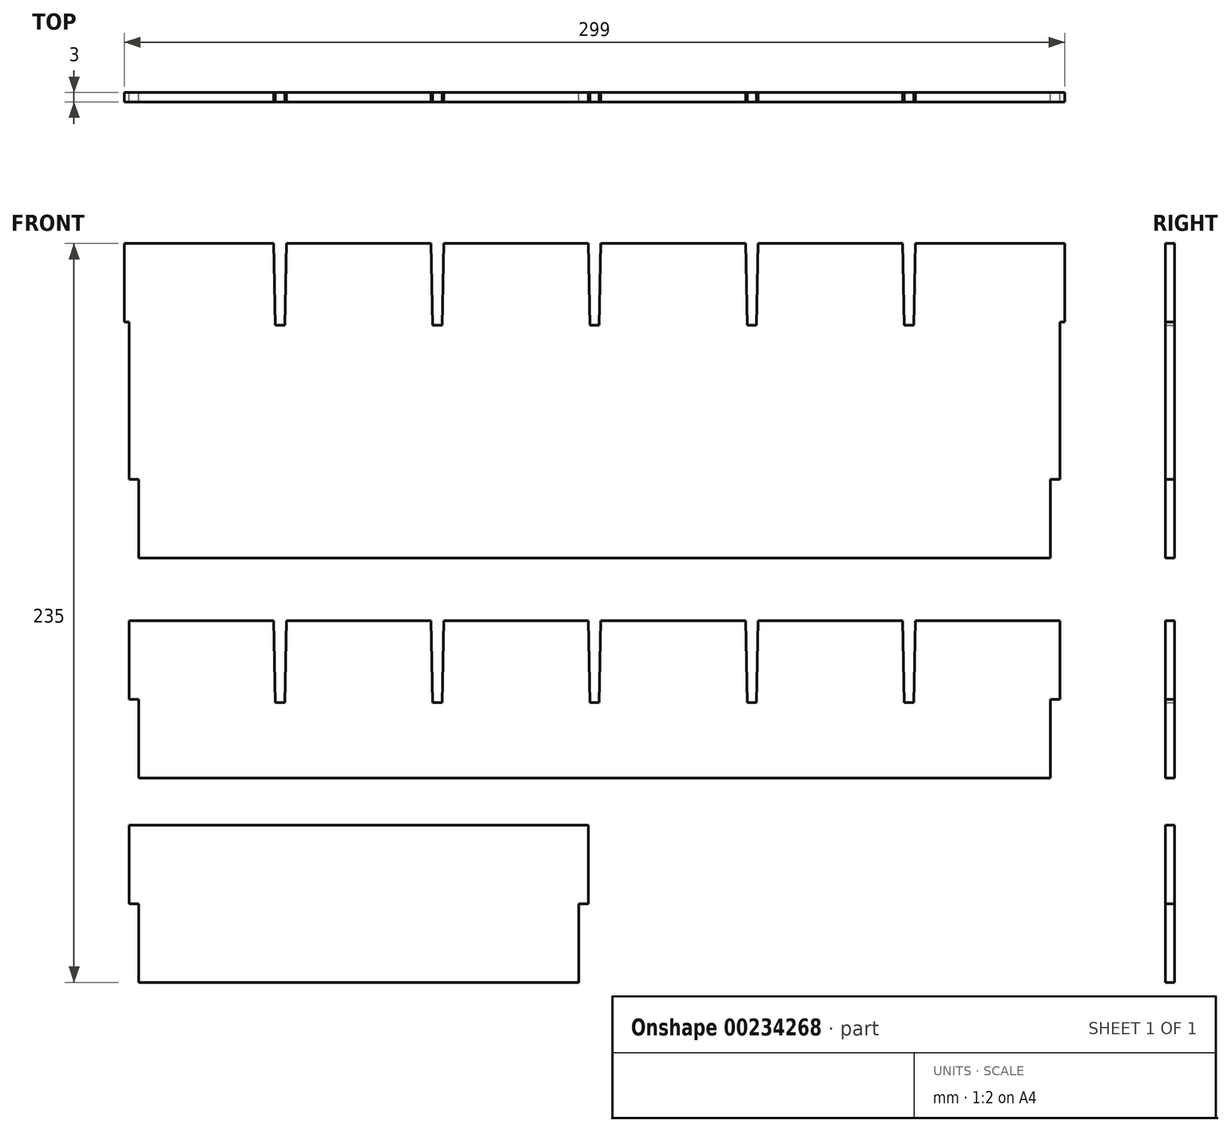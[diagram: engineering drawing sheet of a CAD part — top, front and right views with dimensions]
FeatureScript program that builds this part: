
annotation { "Feature Type Name" : "Feature", "Feature Type Description" : "" }
export const myFeature = defineFeature(function(context is Context, id is Id, definition is map)
    precondition{}
    {
        {
            var Q0;
            Q0=qCreatedBy(makeId("Front.planeOp"),FACE);
            var sketch = newSketch(context, id + "F0", { "sketchPlane" : qUnion([Q0])});
            skLineSegment(sketch, "E0.bottom", {"start": v(10, 10) * mm, "end": v(300, 10) * mm});
            skLineSegment(sketch, "E0.top", {"start": v(10, 110) * mm, "end": v(300, 110) * mm});
            skLineSegment(sketch, "E0.left", {"start": v(10, 10) * mm, "end": v(10, 110) * mm});
            skLineSegment(sketch, "E0.right", {"start": v(300, 10) * mm, "end": v(300, 110) * mm});
            skLineSegment(sketch, "E1", {"start": v(10, 84) * mm, "end": v(300, 84) * mm, "construction": true});
            skLineSegment(sketch, "E2", {"start": v(53, 110) * mm, "end": v(53.5, 84) * mm});
            skLineSegment(sketch, "E3", {"start": v(56.5, 84) * mm, "end": v(57, 110) * mm});
            skLineSegment(sketch, "E4", {"start": v(53, 110) * mm, "end": v(57, 110) * mm});
            skLineSegment(sketch, "E5", {"start": v(53.5, 84) * mm, "end": v(56.5, 84) * mm});
            skPoint(sketch, "E6", {"position": v(55, 110) * mm});
            skPoint(sketch, "E7", {"position": v(55, 84) * mm});
            skPoint(sketch, "E8.1.0.0", {"position": v(105, 110) * mm});
            skLineSegment(sketch, "E8.1.0.1", {"start": v(103, 110) * mm, "end": v(103.5, 84) * mm});
            skLineSegment(sketch, "E8.1.0.2", {"start": v(106.5, 84) * mm, "end": v(107, 110) * mm});
            skPoint(sketch, "E8.1.0.3", {"position": v(105, 84) * mm});
            skLineSegment(sketch, "E8.1.0.4", {"start": v(103, 110) * mm, "end": v(107, 110) * mm});
            skLineSegment(sketch, "E8.1.0.5", {"start": v(103.5, 84) * mm, "end": v(106.5, 84) * mm});
            skPoint(sketch, "E8.2.0.0", {"position": v(155, 110) * mm});
            skLineSegment(sketch, "E8.2.0.1", {"start": v(153, 110) * mm, "end": v(153.5, 84) * mm});
            skLineSegment(sketch, "E8.2.0.2", {"start": v(156.5, 84) * mm, "end": v(157, 110) * mm});
            skPoint(sketch, "E8.2.0.3", {"position": v(155, 84) * mm});
            skLineSegment(sketch, "E8.2.0.4", {"start": v(153, 110) * mm, "end": v(157, 110) * mm});
            skLineSegment(sketch, "E8.2.0.5", {"start": v(153.5, 84) * mm, "end": v(156.5, 84) * mm});
            skPoint(sketch, "E8.3.0.0", {"position": v(205, 110) * mm});
            skLineSegment(sketch, "E8.3.0.1", {"start": v(203, 110) * mm, "end": v(203.5, 84) * mm});
            skLineSegment(sketch, "E8.3.0.2", {"start": v(206.5, 84) * mm, "end": v(207, 110) * mm});
            skPoint(sketch, "E8.3.0.3", {"position": v(205, 84) * mm});
            skLineSegment(sketch, "E8.3.0.4", {"start": v(203, 110) * mm, "end": v(207, 110) * mm});
            skLineSegment(sketch, "E8.3.0.5", {"start": v(203.5, 84) * mm, "end": v(206.5, 84) * mm});
            skPoint(sketch, "E8.4.0.0", {"position": v(255, 110) * mm});
            skLineSegment(sketch, "E8.4.0.1", {"start": v(253, 110) * mm, "end": v(253.5, 84) * mm});
            skLineSegment(sketch, "E8.4.0.2", {"start": v(256.5, 84) * mm, "end": v(257, 110) * mm});
            skPoint(sketch, "E8.4.0.3", {"position": v(255, 84) * mm});
            skLineSegment(sketch, "E8.4.0.4", {"start": v(253, 110) * mm, "end": v(257, 110) * mm});
            skLineSegment(sketch, "E8.4.0.5", {"start": v(253.5, 84) * mm, "end": v(256.5, 84) * mm});
            skLineSegment(sketch, "E8.direction1", {"start": v(53.5, 84) * mm, "end": v(103.5, 84) * mm, "construction": true});
            skPoint(sketch, "E9.oppositeSnap0", {"position": v(10, 60) * mm});
            skLineSegment(sketch, "E9.bottom", {"start": v(10, 110) * mm, "end": v(7, 110) * mm});
            skLineSegment(sketch, "E9.top", {"start": v(10, 60) * mm, "end": v(7, 60) * mm});
            skLineSegment(sketch, "E9.left", {"start": v(10, 110) * mm, "end": v(10, 60) * mm});
            skLineSegment(sketch, "E9.right", {"start": v(7, 110) * mm, "end": v(7, 60) * mm});
            skPoint(sketch, "E10.oppositeSnap0", {"position": v(300, 60) * mm});
            skLineSegment(sketch, "E10.bottom", {"start": v(300, 110) * mm, "end": v(303, 110) * mm});
            skLineSegment(sketch, "E10.top", {"start": v(300, 60) * mm, "end": v(303, 60) * mm});
            skLineSegment(sketch, "E10.left", {"start": v(300, 110) * mm, "end": v(300, 60) * mm});
            skLineSegment(sketch, "E10.right", {"start": v(303, 110) * mm, "end": v(303, 60) * mm});
            skLineSegment(sketch, "E11.bottom", {"start": v(7, 110) * mm, "end": v(5.5, 110) * mm});
            skLineSegment(sketch, "E11.top", {"start": v(7, 85) * mm, "end": v(5.5, 85) * mm});
            skLineSegment(sketch, "E11.left", {"start": v(7, 110) * mm, "end": v(7, 85) * mm});
            skLineSegment(sketch, "E11.right", {"start": v(5.5, 110) * mm, "end": v(5.5, 85) * mm});
            skLineSegment(sketch, "E12.top", {"start": v(10, 35) * mm, "end": v(7, 35) * mm});
            skLineSegment(sketch, "E12.left", {"start": v(10, 60) * mm, "end": v(10, 35) * mm});
            skLineSegment(sketch, "E12.right", {"start": v(7, 60) * mm, "end": v(7, 35) * mm});
            skLineSegment(sketch, "E13.bottom", {"start": v(303, 110) * mm, "end": v(304.5, 110) * mm});
            skLineSegment(sketch, "E13.top", {"start": v(303, 85) * mm, "end": v(304.5, 85) * mm});
            skLineSegment(sketch, "E13.left", {"start": v(303, 110) * mm, "end": v(303, 85) * mm});
            skLineSegment(sketch, "E13.right", {"start": v(304.5, 110) * mm, "end": v(304.5, 85) * mm});
            skLineSegment(sketch, "E14.top", {"start": v(300, 35) * mm, "end": v(303, 35) * mm});
            skLineSegment(sketch, "E14.left", {"start": v(300, 60) * mm, "end": v(300, 35) * mm});
            skLineSegment(sketch, "E14.right", {"start": v(303, 60) * mm, "end": v(303, 35) * mm});
            skSolve(sketch);
        }
        {
            var Q0;
            Q0=makeQuery(id+"F0.imprint","IMPRINT",FACE,{"disambiguationData":[TD([[makeQuery(id+"F0.imprint","IMPRINT",EDGE,{"derivedFrom":sQuery(id+"F0.wireOp",EDGE,"E0.bottom")}),1.0]])]});
            var Q1;
            Q1=makeQuery(id+"F0.imprint","IMPRINT",FACE,{"disambiguationData":[TD([[makeQuery(id+"F0.imprint","IMPRINT",EDGE,{"derivedFrom":sQuery(id+"F0.wireOp",EDGE,"E9.bottom")}),1.0]])]});
            var Q2;
            Q2=makeQuery(id+"F0.imprint","IMPRINT",FACE,{"disambiguationData":[TD([[makeQuery(id+"F0.imprint","IMPRINT",EDGE,{"derivedFrom":sQuery(id+"F0.wireOp",EDGE,"E11.bottom")}),1.0]])]});
            var Q3;
            Q3=makeQuery(id+"F0.imprint","IMPRINT",FACE,{"disambiguationData":[TD([[makeQuery(id+"F0.imprint","IMPRINT",EDGE,{"derivedFrom":sQuery(id+"F0.wireOp",EDGE,"E9.top")}),1.0]])]});
            var Q4;
            Q4=makeQuery(id+"F0.imprint","IMPRINT",FACE,{"disambiguationData":[TD([[makeQuery(id+"F0.imprint","IMPRINT",EDGE,{"derivedFrom":sQuery(id+"F0.wireOp",EDGE,"E10.top")}),-1.0]])]});
            var Q5;
            Q5=makeQuery(id+"F0.imprint","IMPRINT",FACE,{"disambiguationData":[TD([[makeQuery(id+"F0.imprint","IMPRINT",EDGE,{"derivedFrom":sQuery(id+"F0.wireOp",EDGE,"E10.bottom")}),-1.0]])]});
            var Q6;
            Q6=makeQuery(id+"F0.imprint","IMPRINT",FACE,{"disambiguationData":[TD([[makeQuery(id+"F0.imprint","IMPRINT",EDGE,{"derivedFrom":sQuery(id+"F0.wireOp",EDGE,"E13.bottom")}),-1.0]])]});
            extrude(context, id + "F1", {"entities" : qUnion([Q0, Q1, Q2, Q3, Q4, Q5, Q6]), "depth" : 3 * mm});
        }
        {
            var Q0;
            Q0=qCreatedBy(makeId("Front.planeOp"),FACE);
            var sketch = newSketch(context, id + "F2", { "sketchPlane" : qUnion([Q0])});
            skLineSegment(sketch, "E15.bottom", {"start": v(10, -60) * mm, "end": v(300, -60) * mm});
            skLineSegment(sketch, "E15.top", {"start": v(10, -10) * mm, "end": v(300, -10) * mm});
            skLineSegment(sketch, "E15.left", {"start": v(10, -60) * mm, "end": v(10, -10) * mm});
            skLineSegment(sketch, "E15.right", {"start": v(300, -60) * mm, "end": v(300, -10) * mm});
            skLineSegment(sketch, "E16", {"start": v(10, -36) * mm, "end": v(300, -36) * mm, "construction": true});
            skLineSegment(sketch, "E17", {"start": v(53, -10) * mm, "end": v(53.5, -36) * mm});
            skLineSegment(sketch, "E18", {"start": v(56.5, -36) * mm, "end": v(57, -10) * mm});
            skLineSegment(sketch, "E19", {"start": v(53, -10) * mm, "end": v(57, -10) * mm});
            skLineSegment(sketch, "E20", {"start": v(53.5, -36) * mm, "end": v(56.5, -36) * mm});
            skPoint(sketch, "E21", {"position": v(55, -10) * mm});
            skPoint(sketch, "E22", {"position": v(55, -36) * mm});
            skPoint(sketch, "E23.1.0.0", {"position": v(105, -10) * mm});
            skLineSegment(sketch, "E23.1.0.1", {"start": v(103, -10) * mm, "end": v(103.5, -36) * mm});
            skLineSegment(sketch, "E23.1.0.2", {"start": v(106.5, -36) * mm, "end": v(107, -10) * mm});
            skPoint(sketch, "E23.1.0.3", {"position": v(105, -36) * mm});
            skLineSegment(sketch, "E23.1.0.4", {"start": v(103, -10) * mm, "end": v(107, -10) * mm});
            skLineSegment(sketch, "E23.1.0.5", {"start": v(103.5, -36) * mm, "end": v(106.5, -36) * mm});
            skPoint(sketch, "E23.2.0.0", {"position": v(155, -10) * mm});
            skLineSegment(sketch, "E23.2.0.1", {"start": v(153, -10) * mm, "end": v(153.5, -36) * mm});
            skLineSegment(sketch, "E23.2.0.2", {"start": v(156.5, -36) * mm, "end": v(157, -10) * mm});
            skPoint(sketch, "E23.2.0.3", {"position": v(155, -36) * mm});
            skLineSegment(sketch, "E23.2.0.4", {"start": v(153, -10) * mm, "end": v(157, -10) * mm});
            skLineSegment(sketch, "E23.2.0.5", {"start": v(153.5, -36) * mm, "end": v(156.5, -36) * mm});
            skPoint(sketch, "E23.3.0.0", {"position": v(205, -10) * mm});
            skLineSegment(sketch, "E23.3.0.1", {"start": v(203, -10) * mm, "end": v(203.5, -36) * mm});
            skLineSegment(sketch, "E23.3.0.2", {"start": v(206.5, -36) * mm, "end": v(207, -10) * mm});
            skPoint(sketch, "E23.3.0.3", {"position": v(205, -36) * mm});
            skLineSegment(sketch, "E23.3.0.4", {"start": v(203, -10) * mm, "end": v(207, -10) * mm});
            skLineSegment(sketch, "E23.3.0.5", {"start": v(203.5, -36) * mm, "end": v(206.5, -36) * mm});
            skPoint(sketch, "E23.4.0.0", {"position": v(255, -10) * mm});
            skLineSegment(sketch, "E23.4.0.1", {"start": v(253, -10) * mm, "end": v(253.5, -36) * mm});
            skLineSegment(sketch, "E23.4.0.2", {"start": v(256.5, -36) * mm, "end": v(257, -10) * mm});
            skPoint(sketch, "E23.4.0.3", {"position": v(255, -36) * mm});
            skLineSegment(sketch, "E23.4.0.4", {"start": v(253, -10) * mm, "end": v(257, -10) * mm});
            skLineSegment(sketch, "E23.4.0.5", {"start": v(253.5, -36) * mm, "end": v(256.5, -36) * mm});
            skLineSegment(sketch, "E23.direction1", {"start": v(53.5, -36) * mm, "end": v(103.5, -36) * mm, "construction": true});
            skLineSegment(sketch, "E24.bottom", {"start": v(10, -10) * mm, "end": v(7, -10) * mm});
            skLineSegment(sketch, "E24.top", {"start": v(10, -35) * mm, "end": v(7, -35) * mm});
            skLineSegment(sketch, "E24.left", {"start": v(10, -10) * mm, "end": v(10, -35) * mm});
            skLineSegment(sketch, "E24.right", {"start": v(7, -10) * mm, "end": v(7, -35) * mm});
            skLineSegment(sketch, "E25.bottom", {"start": v(300, -10) * mm, "end": v(303, -10) * mm});
            skLineSegment(sketch, "E25.top", {"start": v(300, -35) * mm, "end": v(303, -35) * mm});
            skLineSegment(sketch, "E25.left", {"start": v(300, -10) * mm, "end": v(300, -35) * mm});
            skLineSegment(sketch, "E25.right", {"start": v(303, -10) * mm, "end": v(303, -35) * mm});
            skSolve(sketch);
        }
        {
            var Q0;
            Q0=makeQuery(id+"F2.imprint","IMPRINT",FACE,{"disambiguationData":[TD([[makeQuery(id+"F2.imprint","IMPRINT",EDGE,{"derivedFrom":sQuery(id+"F2.wireOp",EDGE,"E15.bottom")}),1.0]])]});
            var Q1;
            Q1=makeQuery(id+"F2.imprint","IMPRINT",FACE,{"disambiguationData":[TD([[makeQuery(id+"F2.imprint","IMPRINT",EDGE,{"derivedFrom":sQuery(id+"F2.wireOp",EDGE,"E24.bottom")}),1.0]])]});
            var Q2;
            Q2=makeQuery(id+"F2.imprint","IMPRINT",FACE,{"disambiguationData":[TD([[makeQuery(id+"F2.imprint","IMPRINT",EDGE,{"derivedFrom":sQuery(id+"F2.wireOp",EDGE,"E25.bottom")}),-1.0]])]});
            extrude(context, id + "F3", {"entities" : qUnion([Q0, Q1, Q2]), "depth" : 3 * mm});
        }
        {
            var Q0;
            Q0=qCreatedBy(makeId("Front.planeOp"),FACE);
            var sketch = newSketch(context, id + "F4", { "sketchPlane" : qUnion([Q0])});
            skLineSegment(sketch, "E26.bottom", {"start": v(10, -125) * mm, "end": v(150, -125) * mm});
            skLineSegment(sketch, "E26.top", {"start": v(10, -75) * mm, "end": v(150, -75) * mm});
            skLineSegment(sketch, "E26.left", {"start": v(10, -125) * mm, "end": v(10, -75) * mm});
            skLineSegment(sketch, "E26.right", {"start": v(150, -125) * mm, "end": v(150, -75) * mm});
            skLineSegment(sketch, "E27", {"start": v(10, -101) * mm, "end": v(150, -101) * mm, "construction": true});
            skLineSegment(sketch, "E28.bottom", {"start": v(10, -75) * mm, "end": v(7, -75) * mm});
            skLineSegment(sketch, "E28.top", {"start": v(10, -100) * mm, "end": v(7, -100) * mm});
            skLineSegment(sketch, "E28.left", {"start": v(10, -75) * mm, "end": v(10, -100) * mm});
            skLineSegment(sketch, "E28.right", {"start": v(7, -75) * mm, "end": v(7, -100) * mm});
            skLineSegment(sketch, "E29.bottom", {"start": v(150, -75) * mm, "end": v(153, -75) * mm});
            skLineSegment(sketch, "E29.top", {"start": v(150, -100) * mm, "end": v(153, -100) * mm});
            skLineSegment(sketch, "E29.left", {"start": v(150, -75) * mm, "end": v(150, -100) * mm});
            skLineSegment(sketch, "E29.right", {"start": v(153, -75) * mm, "end": v(153, -100) * mm});
            skSolve(sketch);
        }
        {
            var Q0;
            Q0=makeQuery(id+"F4.imprint","IMPRINT",FACE,{"disambiguationData":[TD([[makeQuery(id+"F4.imprint","IMPRINT",EDGE,{"derivedFrom":sQuery(id+"F4.wireOp",EDGE,"E26.bottom")}),1.0]])]});
            var Q1;
            Q1=makeQuery(id+"F4.imprint","IMPRINT",FACE,{"disambiguationData":[TD([[makeQuery(id+"F4.imprint","IMPRINT",EDGE,{"derivedFrom":sQuery(id+"F4.wireOp",EDGE,"E29.bottom")}),-1.0]])]});
            var Q2;
            Q2=makeQuery(id+"F4.imprint","IMPRINT",FACE,{"disambiguationData":[TD([[makeQuery(id+"F4.imprint","IMPRINT",EDGE,{"derivedFrom":sQuery(id+"F4.wireOp",EDGE,"E28.bottom")}),1.0]])]});
            extrude(context, id + "F5", {"entities" : qUnion([Q0, Q1, Q2]), "depth" : 3 * mm});
        }
    });
